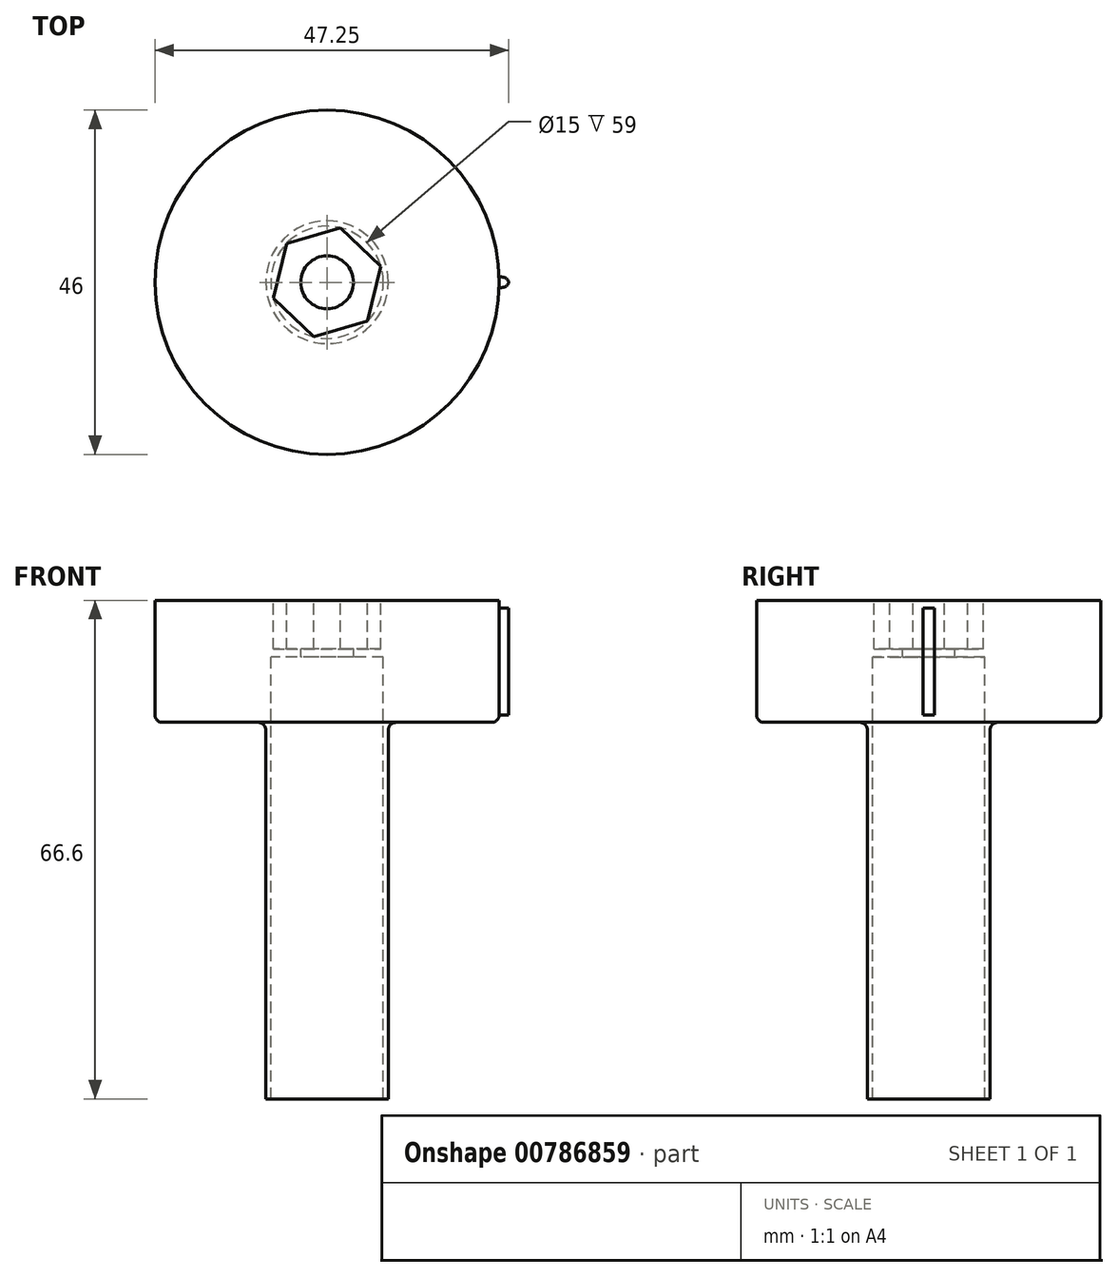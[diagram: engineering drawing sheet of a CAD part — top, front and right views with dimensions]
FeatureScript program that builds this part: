
annotation { "Feature Type Name" : "Feature", "Feature Type Description" : "" }
export const myFeature = defineFeature(function(context is Context, id is Id, definition is map)
    precondition{}
    {
        {
            var Q0;
            Q0=qCreatedBy(makeId("Front.planeOp"),FACE);
            var sketch = newSketch(context, id + "F0", { "sketchPlane" : qUnion([Q0])});
            skLineSegment(sketch, "E0.top", {"start": v(-7.5, -20) * mm, "end": v(7.5, -20) * mm, "construction": true});
            skLineSegment(sketch, "E0.left", {"start": v(-7.5, 7.03) * mm, "end": v(-7.5, -20) * mm});
            skLineSegment(sketch, "E1.0", {"start": v(-8.2, 18.3) * mm, "end": v(-8.2, -20) * mm});
            skLineSegment(sketch, "E2", {"start": v(-8.2, -20) * mm, "end": v(-7.5, -20) * mm});
            skLineSegment(sketch, "E3", {"start": v(-7.5, 17.4) * mm, "end": v(-7.5, 27) * mm});
            skLineSegment(sketch, "E4", {"start": v(0, 16.7) * mm, "end": v(0, 15) * mm});
            skLineSegment(sketch, "E5", {"start": v(-23, 18.3) * mm, "end": v(-23, 28.3) * mm});
            skPoint(sketch, "E6.left.start.orphan", {"position": v(-4.9, 17.77) * mm});
            skPoint(sketch, "E7.orphan", {"position": v(-4.9, 22.23) * mm});
            skPoint(sketch, "E8.orphan", {"position": v(-7.5, 16.7) * mm});
            skLineSegment(sketch, "E9.trimOffspring", {"start": v(-8.2, 18.3) * mm, "end": v(-23, 18.3) * mm});
            skPoint(sketch, "E10.orphan", {"position": v(-4.9, 20) * mm});
            skLineSegment(sketch, "E11.MirrorCS", {"start": v(8.2, -20) * mm, "end": v(7.5, -20) * mm});
            skLineSegment(sketch, "E12.MirrorCS", {"start": v(3.53, 16.7) * mm, "end": v(3.53, 17.4) * mm});
            skLineSegment(sketch, "E13.MirrorCS", {"start": v(7.5, 27) * mm, "end": v(7.5, 28.3) * mm});
            skLineSegment(sketch, "E14.MirrorCS", {"start": v(7.5, 17.4) * mm, "end": v(3.53, 17.4) * mm});
            skLineSegment(sketch, "E15.MirrorCS", {"start": v(3.53, 17.4) * mm, "end": v(7.5, 17.4) * mm});
            skPoint(sketch, "E16.MirrorP", {"position": v(4.9, 22.23) * mm});
            skLineSegment(sketch, "E17.MirrorCS", {"start": v(7.5, 7.03) * mm, "end": v(7.5, -20) * mm});
            skPoint(sketch, "E18.MirrorP", {"position": v(7.5, 16.7) * mm});
            skLineSegment(sketch, "E19.MirrorCS", {"start": v(8.2, 18.3) * mm, "end": v(23, 18.3) * mm});
            skLineSegment(sketch, "E20.MirrorCS", {"start": v(23, 28.3) * mm, "end": v(7.5, 28.3) * mm});
            skPoint(sketch, "E21.MirrorP", {"position": v(4.9, 20) * mm});
            skLineSegment(sketch, "E22.MirrorCS", {"start": v(23, 18.3) * mm, "end": v(23, 28.3) * mm});
            skPoint(sketch, "E23.MirrorP", {"position": v(4.9, 17.77) * mm});
            skLineSegment(sketch, "E24.MirrorCS", {"start": v(7.5, 17.4) * mm, "end": v(7.5, 27) * mm});
            skLineSegment(sketch, "E25.MirrorCS", {"start": v(8.2, 18.3) * mm, "end": v(8.2, -20) * mm});
            skLineSegment(sketch, "E26.MirrorCS", {"start": v(5.36, 15) * mm, "end": v(7.5, 7.03) * mm});
            skLineSegment(sketch, "E27.MirrorCS", {"start": v(0, 15) * mm, "end": v(5.36, 15) * mm});
            skPoint(sketch, "E28.MirrorCS.end.orphan", {"position": v(3.53, 16.7) * mm});
            skPoint(sketch, "E28.MirrorCS.start.orphan", {"position": v(0, 16.7) * mm});
            skLineSegment(sketch, "E29.top", {"start": v(-7.5, 27) * mm, "end": v(-3.53, 27) * mm});
            skLineSegment(sketch, "E29.right", {"start": v(-3.53, 28.3) * mm, "end": v(-3.53, 27) * mm});
            skLineSegment(sketch, "E30", {"start": v(-7.5, 17.4) * mm, "end": v(-7.5, 7.03) * mm});
            skPoint(sketch, "E31.end.orphan", {"position": v(-5.36, 15) * mm});
            skPoint(sketch, "E32.left.end.orphan", {"position": v(-3.53, 17.4) * mm});
            skPoint(sketch, "E32.left.start.orphan", {"position": v(-3.53, 16.7) * mm});
            skLineSegment(sketch, "E33", {"start": v(-23, 28.3) * mm, "end": v(-23, 34.6) * mm});
            skLineSegment(sketch, "E34", {"start": v(-23, 34.6) * mm, "end": v(-3.53, 34.6) * mm});
            skLineSegment(sketch, "E35.right", {"start": v(-3.53, 28.3) * mm, "end": v(-3.53, 34.6) * mm});
            skPoint(sketch, "E29.bottom.start.orphan", {"position": v(-7.5, 28.3) * mm});
            skLineSegment(sketch, "E36", {"start": v(0, 16.7) * mm, "end": v(0, 34.77) * mm});
            skLineSegment(sketch, "E37.top", {"start": v(-8.2, -32) * mm, "end": v(-7.5, -32) * mm});
            skLineSegment(sketch, "E37.left", {"start": v(-8.2, -20) * mm, "end": v(-8.2, -32) * mm});
            skLineSegment(sketch, "E37.right", {"start": v(-7.5, -20) * mm, "end": v(-7.5, -32) * mm});
            skSolve(sketch);
        }
        {
            var Q0;
            Q0=makeQuery(id+"F0.imprint","IMPRINT",FACE,{"disambiguationData":[TD([[makeQuery(id+"F0.imprint","IMPRINT",EDGE,{"derivedFrom":sQuery(id+"F0.wireOp",EDGE,"E0.left")}),-1.0]])]});
            var Q1;
            Q1=makeQuery(id+"F0.imprint","IMPRINT",FACE,{"disambiguationData":[TD([[makeQuery(id+"F0.imprint","IMPRINT",EDGE,{"derivedFrom":sQuery(id+"F0.wireOp",EDGE,"E2")}),-1.0]])]});
            var Q2;
            Q2=sQuery(id+"F0.wireOp",EDGE,"E4");
            revolve(context, id + "F1", {"surfaceOperationType" : NewSurfaceOperationType.NEW, "entities" : qUnion([Q0, Q1]), "axis" : qUnion([Q2]), "revolveType" : RevolveType.FULL});
        }
        {
            var Q0;
            Q0=makeQuery(id+"F1.opRevolve","SWEPT_EDGE",EDGE,{"disambiguationData":[OSD([sQuery(id+"F0.wireOp",EDGE,"E1.0"),sQuery(id+"F0.wireOp",EDGE,"E9.trimOffspring")])]});
            var Q1;
            Q1=makeQuery(id+"F1.opRevolve","SWEPT_EDGE",EDGE,{"disambiguationData":[OSD([sQuery(id+"F0.wireOp",EDGE,"E5"),sQuery(id+"F0.wireOp",EDGE,"E9.trimOffspring")])]});
            var Q2;
            Q2=makeQuery(id+"F1.opRevolve","SWEPT_EDGE",EDGE,{"disambiguationData":[OSD([sQuery(id+"F0.wireOp",EDGE,"E5"),sQuery(id+"F0.wireOp",EDGE,"1doxyCWQ-vjGX-KyjE-E3ru-lWZ0XpCGLjJG")])]});
            var Q3;
            Q3=makeQuery(id+"F1.opRevolve","SWEPT_EDGE",EDGE,{"disambiguationData":[OSD([sQuery(id+"F0.wireOp",EDGE,"1doxyCWQ-vjGX-KyjE-E3ru-lWZ0XpCGLjJG"),sQuery(id+"F0.wireOp",EDGE,"hwmKKzMA-YaXV-Vb3W-40vX-lfPw4ARgg1NP")])]});
            fillet(context, id + "F2", {"entities" : qUnion([Q0, Q1, Q2, Q3]), "radius" : 1 * mm, "tangentPropagation" : true, "allowEdgeOverflow" : false});
        }
        {
            var Q0;
            Q0=makeQuery(id+"F1.opRevolve","SWEPT_FACE",FACE,{"disambiguationData":[OSD([sQuery(id+"F0.wireOp",EDGE,"E34")])]});
            cPlane(context, id + "F3", {"entities" : qUnion([Q0]), "cplaneType" : CPlaneType.OFFSET, "offset" : 1 * mm, "oppositeDirection" : true, "width" : 150 * mm, "height" : 150 * mm});
        }
        {
            var Q0;
            Q0=qCreatedBy(id+"F3.planeOp",FACE);
            var sketch = newSketch(context, id + "F4", { "sketchPlane" : qUnion([Q0])});
            skEllipse(sketch, "E38", {"center": v(23, 0) * mm, "majorRadius": 1.25 * mm, "minorRadius": 0.75 * mm, "majorAxis": v(1, 0)});
            skSolve(sketch);
        }
        {
            var Q0;
            Q0=makeQuery(id+"F4.imprint","IMPRINT",FACE,{"disambiguationData":[TD([[makeQuery(id+"F4.imprint","IMPRINT",EDGE,{"derivedFrom":sQuery(id+"F4.wireOp",EDGE,"E38")}),1.0]])]});
            extrude(context, id + "F5", {"entities" : qUnion([Q0]), "operationType" : NewBodyOperationType.ADD, "oppositeDirection" : true, "depth" : 14.3 * mm, "offsetDistance" : 25 * mm});
        }
        {
            var Q0;
            Q0=makeQuery(id+"F1.opRevolve","SWEPT_FACE",FACE,{"disambiguationData":[OSD([sQuery(id+"F0.wireOp",EDGE,"E34")])]});
            var sketch = newSketch(context, id + "F6", { "sketchPlane" : qUnion([Q0])});
            skCircle(sketch, "E39.cCircle", {"center": v(0, 0) * mm, "radius": 6.5 * mm, "construction": true});
            skLineSegment(sketch, "E39.0", {"start": v(-1.78, -7.3) * mm, "end": v(-7.2, -2.1) * mm});
            skLineSegment(sketch, "E39.1", {"start": v(-7.2, -2.1) * mm, "end": v(-5.43, 5.18) * mm});
            skLineSegment(sketch, "E39.2", {"start": v(-5.43, 5.18) * mm, "end": v(1.78, 7.3) * mm});
            skLineSegment(sketch, "E39.3", {"start": v(1.78, 7.3) * mm, "end": v(7.2, 2.1) * mm});
            skLineSegment(sketch, "E39.4", {"start": v(7.2, 2.1) * mm, "end": v(5.43, -5.18) * mm});
            skLineSegment(sketch, "E39.5", {"start": v(5.43, -5.18) * mm, "end": v(-1.78, -7.3) * mm});
            skPoint(sketch, "E39.0.midPoint", {"position": v(-4.49, -4.7) * mm});
            skSolve(sketch);
        }
        {
            var Q0;
            Q0=makeQuery(id+"F6.imprint","IMPRINT",FACE,{"disambiguationData":[TD([[makeQuery(id+"F6.imprint","IMPRINT",EDGE,{"derivedFrom":sQuery(id+"F6.wireOp",EDGE,"E39.0")}),-1.0]])]});
            extrude(context, id + "F7", {"entities" : qUnion([Q0]), "operationType" : NewBodyOperationType.REMOVE, "oppositeDirection" : true, "depth" : 6.5 * mm, "offsetDistance" : 25 * mm});
        }
    });
